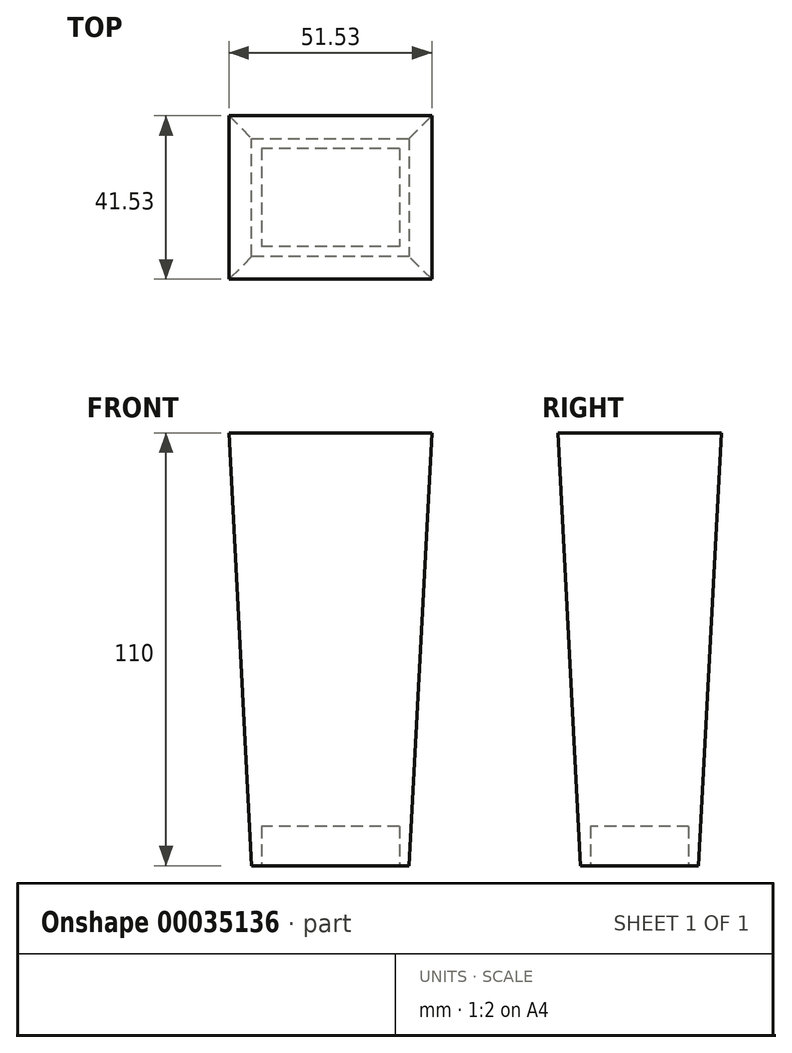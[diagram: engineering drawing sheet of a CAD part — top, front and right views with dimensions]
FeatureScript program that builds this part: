
annotation { "Feature Type Name" : "Feature", "Feature Type Description" : "" }
export const myFeature = defineFeature(function(context is Context, id is Id, definition is map)
    precondition{}
    {
        {
            var Q0;
            Q0=qCreatedBy(makeId("Top.planeOp"),FACE);
            var sketch = newSketch(context, id + "F0", { "sketchPlane" : qUnion([Q0])});
            skLineSegment(sketch, "E0.bottom", {"start": v(-50.05, -73) * mm, "end": v(-10.05, -73) * mm});
            skLineSegment(sketch, "E0.top", {"start": v(-50.05, -43) * mm, "end": v(-10.05, -43) * mm});
            skLineSegment(sketch, "E0.left", {"start": v(-50.05, -73) * mm, "end": v(-50.05, -43) * mm});
            skLineSegment(sketch, "E0.right", {"start": v(-10.05, -73) * mm, "end": v(-10.05, -43) * mm});
            skSolve(sketch);
        }
        {
            var Q0;
            Q0=makeQuery(id+"F0.imprint","IMPRINT",FACE,{"disambiguationData":[TD([[makeQuery(id+"F0.imprint","IMPRINT",EDGE,{"derivedFrom":sQuery(id+"F0.wireOp",EDGE,"E0.bottom")}),1.0]])]});
            extrude(context, id + "F1", {"entities" : qUnion([Q0]), "depth" : 110 * mm, "hasDraft" : true, "draftAngle" : 3 * degree});
        }
        {
            var Q0;
            Q0=makeQuery(id+"F1.opExtrude","CAP_FACE",FACE,{"disambiguationData":[OSD([sQuery(id+"F0.wireOp",EDGE,"E0.bottom"),sQuery(id+"F0.wireOp",EDGE,"E0.top"),sQuery(id+"F0.wireOp",EDGE,"E0.left"),sQuery(id+"F0.wireOp",EDGE,"E0.right")])],"isStart":true});
            var sketch = newSketch(context, id + "F2", { "sketchPlane" : qUnion([Q0])});
            skLineSegment(sketch, "E1.rect.bottom", {"start": v(-12.55, 45.5) * mm, "end": v(-47.55, 45.5) * mm});
            skLineSegment(sketch, "E1.rect.top", {"start": v(-12.55, 70.5) * mm, "end": v(-47.55, 70.5) * mm});
            skLineSegment(sketch, "E1.rect.left", {"start": v(-12.55, 45.5) * mm, "end": v(-12.55, 70.5) * mm});
            skLineSegment(sketch, "E1.rect.right", {"start": v(-47.55, 45.5) * mm, "end": v(-47.55, 70.5) * mm});
            skPoint(sketch, "E1.rect.middle", {"position": v(-30.05, 58) * mm});
            skPoint(sketch, "E1.rect.middle.positionSnap0", {"position": v(-10.05, 58) * mm});
            skPoint(sketch, "E1.rect.middle.positionSnap1", {"position": v(-30.05, 73) * mm});
            skPoint(sketch, "E1.rect.centerSnap0", {"position": v(-10.05, 58) * mm});
            skPoint(sketch, "E1.rect.centerSnap1", {"position": v(-30.05, 73) * mm});
            skSolve(sketch);
        }
        {
            var Q0;
            Q0 = qSketchRegion(id + "F2", true);
            extrude(context, id + "F3", {"entities" : qUnion([Q0]), "operationType" : NewBodyOperationType.REMOVE, "oppositeDirection" : true, "depth" : 10 * mm});
        }
    });
